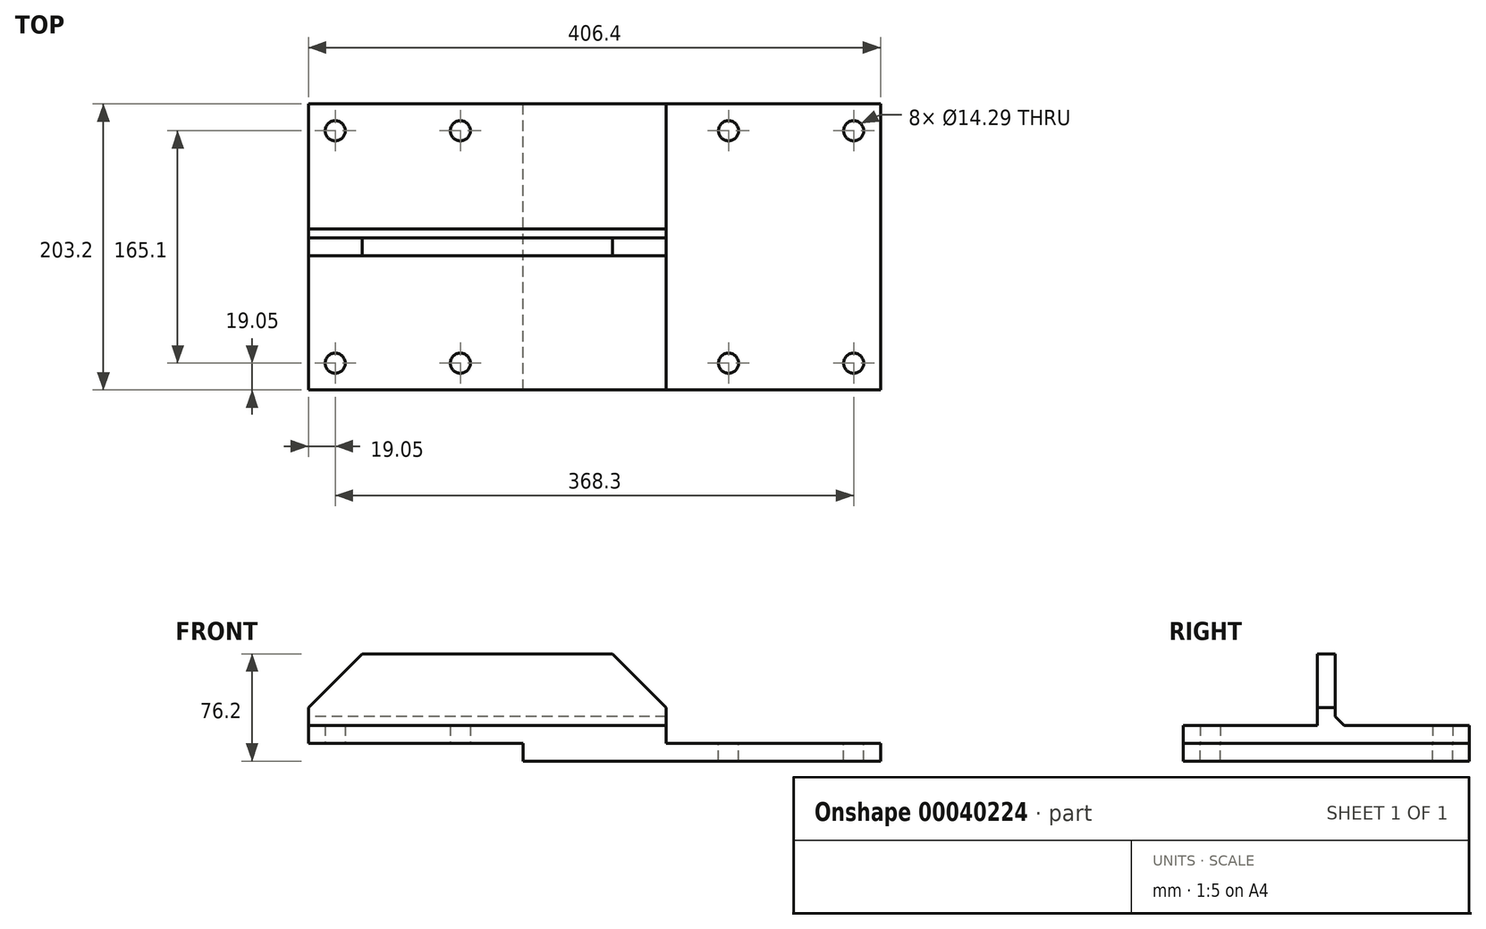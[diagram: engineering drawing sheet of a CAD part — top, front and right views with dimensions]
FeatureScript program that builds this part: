
annotation { "Feature Type Name" : "Feature", "Feature Type Description" : "" }
export const myFeature = defineFeature(function(context is Context, id is Id, definition is map)
    precondition{}
    {
        {
            var Q0;
            Q0=qCreatedBy(makeId("Top.planeOp"),FACE);
            var sketch = newSketch(context, id + "F0", { "sketchPlane" : qUnion([Q0])});
            skLineSegment(sketch, "E0", {"start": v(0, 106.75) * mm, "end": v(0, -105.6) * mm, "construction": true});
            skLineSegment(sketch, "E1.0", {"start": v(-203.2, 106.75) * mm, "end": v(-203.2, -105.6) * mm, "construction": true});
            skLineSegment(sketch, "E2.MirrorCS", {"start": v(203.2, 106.75) * mm, "end": v(203.2, -105.6) * mm, "construction": true});
            skLineSegment(sketch, "E3", {"start": v(-283.64, 0) * mm, "end": v(308.6, 0) * mm, "construction": true});
            skLineSegment(sketch, "E4.0", {"start": v(-283.64, -101.6) * mm, "end": v(308.6, -101.6) * mm, "construction": true});
            skLineSegment(sketch, "E5.bottom", {"start": v(-203.2, -101.6) * mm, "end": v(50.8, -101.6) * mm});
            skLineSegment(sketch, "E5.top", {"start": v(-203.2, 101.6) * mm, "end": v(50.8, 101.6) * mm});
            skLineSegment(sketch, "E5.left", {"start": v(-203.2, -101.6) * mm, "end": v(-203.2, 101.6) * mm});
            skLineSegment(sketch, "E5.right", {"start": v(50.8, -101.6) * mm, "end": v(50.8, 101.6) * mm});
            skLineSegment(sketch, "E6.0", {"start": v(-139.7, -101.6) * mm, "end": v(-139.7, 101.6) * mm, "construction": true});
            skLineSegment(sketch, "E7.0", {"start": v(-184.15, -101.6) * mm, "end": v(-184.15, 101.6) * mm, "construction": true});
            skLineSegment(sketch, "E8.0", {"start": v(-283.64, -82.55) * mm, "end": v(308.6, -82.55) * mm, "construction": true});
            skCircle(sketch, "E9", {"center": v(-184.15, -82.55) * mm, "radius": 7.14 * mm});
            skCircle(sketch, "E10.MirrorC", {"center": v(-95.25, -82.55) * mm, "radius": 7.14 * mm});
            skCircle(sketch, "E11.MirrorC", {"center": v(-95.25, 82.55) * mm, "radius": 7.14 * mm});
            skCircle(sketch, "E12.MirrorC", {"center": v(-184.15, 82.55) * mm, "radius": 7.14 * mm});
            skSolve(sketch);
        }
        {
            var Q0;
            Q0=makeQuery(id+"F0.imprint","IMPRINT",FACE,{"disambiguationData":[TD([[makeQuery(id+"F0.imprint","IMPRINT",EDGE,{"derivedFrom":sQuery(id+"F0.wireOp",EDGE,"E5.bottom")}),1.0]])]});
            extrude(context, id + "F1", {"entities" : qUnion([Q0]), "depth" : 12.7 * mm});
        }
        {
            var Q0;
            Q0=makeQuery(id+"F1.opExtrude","CAP_FACE",FACE,{"disambiguationData":[OSD([sQuery(id+"F0.wireOp",EDGE,"E5.bottom"),sQuery(id+"F0.wireOp",EDGE,"E5.top"),sQuery(id+"F0.wireOp",EDGE,"E5.left"),sQuery(id+"F0.wireOp",EDGE,"E5.right"),sQuery(id+"F0.wireOp",EDGE,"E9"),sQuery(id+"F0.wireOp",EDGE,"E10.MirrorC"),sQuery(id+"F0.wireOp",EDGE,"E11.MirrorC"),sQuery(id+"F0.wireOp",EDGE,"E12.MirrorC")])],"isStart":true});
            var sketch = newSketch(context, id + "F2", { "sketchPlane" : qUnion([Q0])});
            skLineSegment(sketch, "E13.0", {"start": v(-283.64, 101.6) * mm, "end": v(308.6, 101.6) * mm, "construction": true});
            skLineSegment(sketch, "E14.0", {"start": v(203.2, -106.75) * mm, "end": v(203.2, 105.6) * mm, "construction": true});
            skLineSegment(sketch, "E15.bottom", {"start": v(203.2, 101.6) * mm, "end": v(-50.8, 101.6) * mm});
            skLineSegment(sketch, "E15.top", {"start": v(203.2, -101.6) * mm, "end": v(-50.8, -101.6) * mm});
            skLineSegment(sketch, "E15.left", {"start": v(203.2, 101.6) * mm, "end": v(203.2, -101.6) * mm});
            skLineSegment(sketch, "E15.right", {"start": v(-50.8, 101.6) * mm, "end": v(-50.8, -101.6) * mm});
            skLineSegment(sketch, "E16.0", {"start": v(139.7, 101.6) * mm, "end": v(139.7, -101.6) * mm, "construction": true});
            skLineSegment(sketch, "E17.0", {"start": v(184.15, 101.6) * mm, "end": v(184.15, -101.6) * mm, "construction": true});
            skLineSegment(sketch, "E18.0", {"start": v(-283.64, 82.55) * mm, "end": v(308.6, 82.55) * mm, "construction": true});
            skCircle(sketch, "E19", {"center": v(184.15, 82.55) * mm, "radius": 7.14 * mm});
            skCircle(sketch, "E20.MirrorC", {"center": v(95.25, 82.55) * mm, "radius": 7.14 * mm});
            skCircle(sketch, "E21.MirrorC", {"center": v(95.25, -82.55) * mm, "radius": 7.14 * mm});
            skCircle(sketch, "E22.MirrorC", {"center": v(184.15, -82.55) * mm, "radius": 7.14 * mm});
            skSolve(sketch);
        }
        {
            var Q0;
            Q0=qSketchRegion(id+"F2",true);
            extrude(context, id + "F3", {"entities" : qUnion([Q0]), "depth" : 12.7 * mm});
        }
        {
            var Q0;
            Q0=makeQuery(id+"F1.opExtrude","CAP_FACE",FACE,{"disambiguationData":[OSD([sQuery(id+"F0.wireOp",EDGE,"E5.bottom"),sQuery(id+"F0.wireOp",EDGE,"E5.top"),sQuery(id+"F0.wireOp",EDGE,"E5.left"),sQuery(id+"F0.wireOp",EDGE,"E5.right"),sQuery(id+"F0.wireOp",EDGE,"E9"),sQuery(id+"F0.wireOp",EDGE,"E10.MirrorC"),sQuery(id+"F0.wireOp",EDGE,"E11.MirrorC"),sQuery(id+"F0.wireOp",EDGE,"E12.MirrorC")])],"isStart":false});
            var sketch = newSketch(context, id + "F4", { "sketchPlane" : qUnion([Q0])});
            skLineSegment(sketch, "E23.0", {"start": v(-283.64, 0) * mm, "end": v(308.6, 0) * mm, "construction": true});
            skLineSegment(sketch, "E24.0", {"start": v(-203.2, -6.35) * mm, "end": v(50.8, -6.35) * mm});
            skLineSegment(sketch, "E25.0", {"start": v(-203.2, -6.35) * mm, "end": v(-203.2, 6.35) * mm});
            skLineSegment(sketch, "E26.0", {"start": v(50.8, -6.35) * mm, "end": v(50.8, 6.35) * mm});
            skLineSegment(sketch, "E27.MirrorCS", {"start": v(-203.2, 6.35) * mm, "end": v(50.8, 6.35) * mm});
            skPoint(sketch, "E28.orphan", {"position": v(-283.64, 6.35) * mm});
            skPoint(sketch, "E29.orphan", {"position": v(-283.64, -6.35) * mm});
            skPoint(sketch, "E30.orphan", {"position": v(308.6, 6.35) * mm});
            skPoint(sketch, "E31.orphan", {"position": v(308.6, -6.35) * mm});
            skPoint(sketch, "E32.orphan", {"position": v(50.8, 101.6) * mm});
            skPoint(sketch, "E33.orphan", {"position": v(50.8, -101.6) * mm});
            skPoint(sketch, "E34.orphan", {"position": v(-203.2, -101.6) * mm});
            skPoint(sketch, "E35.orphan", {"position": v(-203.2, 101.6) * mm});
            skSolve(sketch);
        }
        {
            var Q0;
            Q0=qSketchRegion(id+"F4",true);
            extrude(context, id + "F5", {"entities" : qUnion([Q0]), "depth" : 50.8 * mm});
        }
        {
            var Q0;
            Q0=makeQuery(id+"F5.opExtrude","CAP_EDGE",EDGE,{"disambiguationData":[OSD([sQuery(id+"F4.wireOp",EDGE,"E25.0")])],"isStart":false});
            var Q1;
            Q1=makeQuery(id+"F5.opExtrude","CAP_EDGE",EDGE,{"disambiguationData":[OSD([sQuery(id+"F4.wireOp",EDGE,"E26.0")])],"isStart":false});
            chamfer(context, id + "F6", {"entities" : qUnion([Q0, Q1]), "width" : 38.1 * mm, "tangentPropagation" : true});
        }
        {
            var Q0;
            Q0=makeQuery(id+"F3.opExtrude","CAP_FACE",FACE,{"disambiguationData":[OSD([sQuery(id+"F2.wireOp",EDGE,"E15.bottom"),sQuery(id+"F2.wireOp",EDGE,"E15.top"),sQuery(id+"F2.wireOp",EDGE,"E15.left"),sQuery(id+"F2.wireOp",EDGE,"E15.right"),sQuery(id+"F2.wireOp",EDGE,"E19"),sQuery(id+"F2.wireOp",EDGE,"E20.MirrorC"),sQuery(id+"F2.wireOp",EDGE,"E21.MirrorC"),sQuery(id+"F2.wireOp",EDGE,"E22.MirrorC")])],"isStart":false});
            var sketch = newSketch(context, id + "F7", { "sketchPlane" : qUnion([Q0])});
            skLineSegment(sketch, "E36.0", {"start": v(-283.64, 0) * mm, "end": v(308.6, 0) * mm, "construction": true});
            skLineSegment(sketch, "E37.0", {"start": v(-50.8, 101.6) * mm, "end": v(-50.8, -101.6) * mm});
            skLineSegment(sketch, "E38.0", {"start": v(203.2, -106.75) * mm, "end": v(203.2, 105.6) * mm});
            skLineSegment(sketch, "E39.0", {"start": v(-283.64, -6.35) * mm, "end": v(308.6, -6.35) * mm});
            skLineSegment(sketch, "E40.MirrorCS", {"start": v(-283.64, 6.35) * mm, "end": v(308.6, 6.35) * mm});
            skSolve(sketch);
        }
        {
            var Q0;
            {var subQ0=sQuery(id+"F7.wireOp",EDGE,"E40.MirrorCS");var subQ3=sQuery(id+"F7.wireOp",EDGE,"E37.0");var subQ4=makeQuery(id+"F7.imprint","INTERSECT",VERTEX,{"derivedFrom":[subQ3,subQ0]});Q0=makeQuery(id+"F7.imprint","IMPRINT",FACE,{"disambiguationData":[TD([[makeQuery(id+"F7.imprint","IMPRINT",EDGE,{"disambiguationData":[TD([[subQ4,-1.0]])],"derivedFrom":subQ3}),1.0]])]});}
            extrude(context, id + "F8", {"entities" : qUnion([Q0]), "depth" : 50.8 * mm});
        }
        {
            var Q0;
            Q0=makeQuery(id+"F8.opExtrude","CAP_EDGE",EDGE,{"disambiguationData":[OSD([sQuery(id+"F7.wireOp",EDGE,"E38.0")])],"isStart":false});
            var Q1;
            Q1=makeQuery(id+"F8.opExtrude","CAP_EDGE",EDGE,{"disambiguationData":[OSD([sQuery(id+"F7.wireOp",EDGE,"E37.0")])],"isStart":false});
            chamfer(context, id + "F9", {"entities" : qUnion([Q0, Q1]), "width" : 38.1 * mm, "tangentPropagation" : true});
        }
        {
            var Q0;
            Q0=makeQuery(id+"F1.opExtrude","SWEPT_BODY",BODY,{"disambiguationData":[OSD([sQuery(id+"F0.wireOp",EDGE,"E5.bottom"),sQuery(id+"F0.wireOp",EDGE,"E5.top"),sQuery(id+"F0.wireOp",EDGE,"E5.left"),sQuery(id+"F0.wireOp",EDGE,"E5.right"),sQuery(id+"F0.wireOp",EDGE,"E9"),sQuery(id+"F0.wireOp",EDGE,"E10.MirrorC"),sQuery(id+"F0.wireOp",EDGE,"E11.MirrorC"),sQuery(id+"F0.wireOp",EDGE,"E12.MirrorC")])]});
            var Q1;
            Q1=makeQuery(id+"F5.opExtrude","SWEPT_BODY",BODY,{"disambiguationData":[OSD([sQuery(id+"F4.wireOp",EDGE,"E24.0"),sQuery(id+"F4.wireOp",EDGE,"E25.0"),sQuery(id+"F4.wireOp",EDGE,"E26.0"),sQuery(id+"F4.wireOp",EDGE,"E27.MirrorCS")])]});
            var Q2;
            Q2=makeQuery(id+"F3.opExtrude","SWEPT_BODY",BODY,{"disambiguationData":[OSD([sQuery(id+"F2.wireOp",EDGE,"E15.bottom"),sQuery(id+"F2.wireOp",EDGE,"E15.top"),sQuery(id+"F2.wireOp",EDGE,"E15.left"),sQuery(id+"F2.wireOp",EDGE,"E15.right"),sQuery(id+"F2.wireOp",EDGE,"E19"),sQuery(id+"F2.wireOp",EDGE,"E20.MirrorC"),sQuery(id+"F2.wireOp",EDGE,"E21.MirrorC"),sQuery(id+"F2.wireOp",EDGE,"E22.MirrorC")])]});
            var Q3;
            Q3=makeQuery(id+"F8.opExtrude","SWEPT_BODY",BODY,{"disambiguationData":[OSD([sQuery(id+"F7.wireOp",EDGE,"E37.0"),sQuery(id+"F7.wireOp",EDGE,"E38.0"),sQuery(id+"F7.wireOp",EDGE,"E39.0"),sQuery(id+"F7.wireOp",EDGE,"E40.MirrorCS")])]});
            booleanBodies(context, id + "F10", {"operationType" : BooleanOperationType.UNION, "tools" : qUnion([Q0, Q1, Q2, Q3])});
        }
        {
            var Q0;
            Q0=makeQuery(id+"F1.opExtrude","CAP_EDGE",EDGE,{"disambiguationData":[OSD([sQuery(id+"F0.wireOp",EDGE,"E5.right")])],"isStart":true});
            var Q1;
            Q1=makeQuery(id+"F5.opExtrude","CAP_EDGE",EDGE,{"disambiguationData":[OSD([sQuery(id+"F4.wireOp",EDGE,"E24.0")])],"isStart":true});
            var Q2;
            Q2=makeQuery(id+"F5.opExtrude","CAP_EDGE",EDGE,{"disambiguationData":[OSD([sQuery(id+"F4.wireOp",EDGE,"E27.MirrorCS")])],"isStart":true});
            var Q3;
            Q3=makeQuery(id+"F3.opExtrude","CAP_EDGE",EDGE,{"disambiguationData":[OSD([sQuery(id+"F2.wireOp",EDGE,"E15.right")])],"isStart":true});
            var Q4;
            Q4=makeQuery(id+"F8.opExtrude","CAP_EDGE",EDGE,{"disambiguationData":[OSD([sQuery(id+"F7.wireOp",EDGE,"E39.0")])],"isStart":true});
            var Q5;
            Q5=makeQuery(id+"F8.opExtrude","CAP_EDGE",EDGE,{"disambiguationData":[OSD([sQuery(id+"F7.wireOp",EDGE,"E40.MirrorCS")])],"isStart":true});
            chamfer(context, id + "F11", {"entities" : qUnion([Q0, Q1, Q2, Q3, Q4, Q5]), "width" : 6.35 * mm, "tangentPropagation" : true});
        }
        {
            var Q0;
            Q0=makeQuery(id+"F10.opBoolean","MERGE",FACE,{"derivedFrom":[makeQuery(id+"F1.opExtrude","SWEPT_FACE",FACE,{"disambiguationData":[OSD([sQuery(id+"F0.wireOp",EDGE,"E5.bottom")])]}),makeQuery(id+"F3.opExtrude","SWEPT_FACE",FACE,{"disambiguationData":[OSD([sQuery(id+"F2.wireOp",EDGE,"E15.bottom")])]})]});
            var sketch = newSketch(context, id + "F12", { "sketchPlane" : qUnion([Q0])});
            skLineSegment(sketch, "E41.0", {"start": v(-50.8, -12.7) * mm, "end": v(203.2, -12.7) * mm, "construction": true});
            skLineSegment(sketch, "E42.bottom", {"start": v(-50.8, -12.7) * mm, "end": v(239.74, -12.7) * mm});
            skLineSegment(sketch, "E42.top", {"start": v(-50.8, -113.87) * mm, "end": v(239.74, -113.87) * mm});
            skLineSegment(sketch, "E42.left", {"start": v(-50.8, -12.7) * mm, "end": v(-50.8, -113.87) * mm});
            skLineSegment(sketch, "E42.right", {"start": v(239.74, -12.7) * mm, "end": v(239.74, -113.87) * mm});
            skSolve(sketch);
        }
        {
            var Q0;
            Q0 = qSketchRegion(id + "F12", true);
            extrude(context, id + "F13", {"entities" : qUnion([Q0]), "operationType" : NewBodyOperationType.REMOVE, "endBound" : BoundingType.THROUGH_ALL, "oppositeDirection" : true, "depth" : 25.4 * mm});
        }
    });
